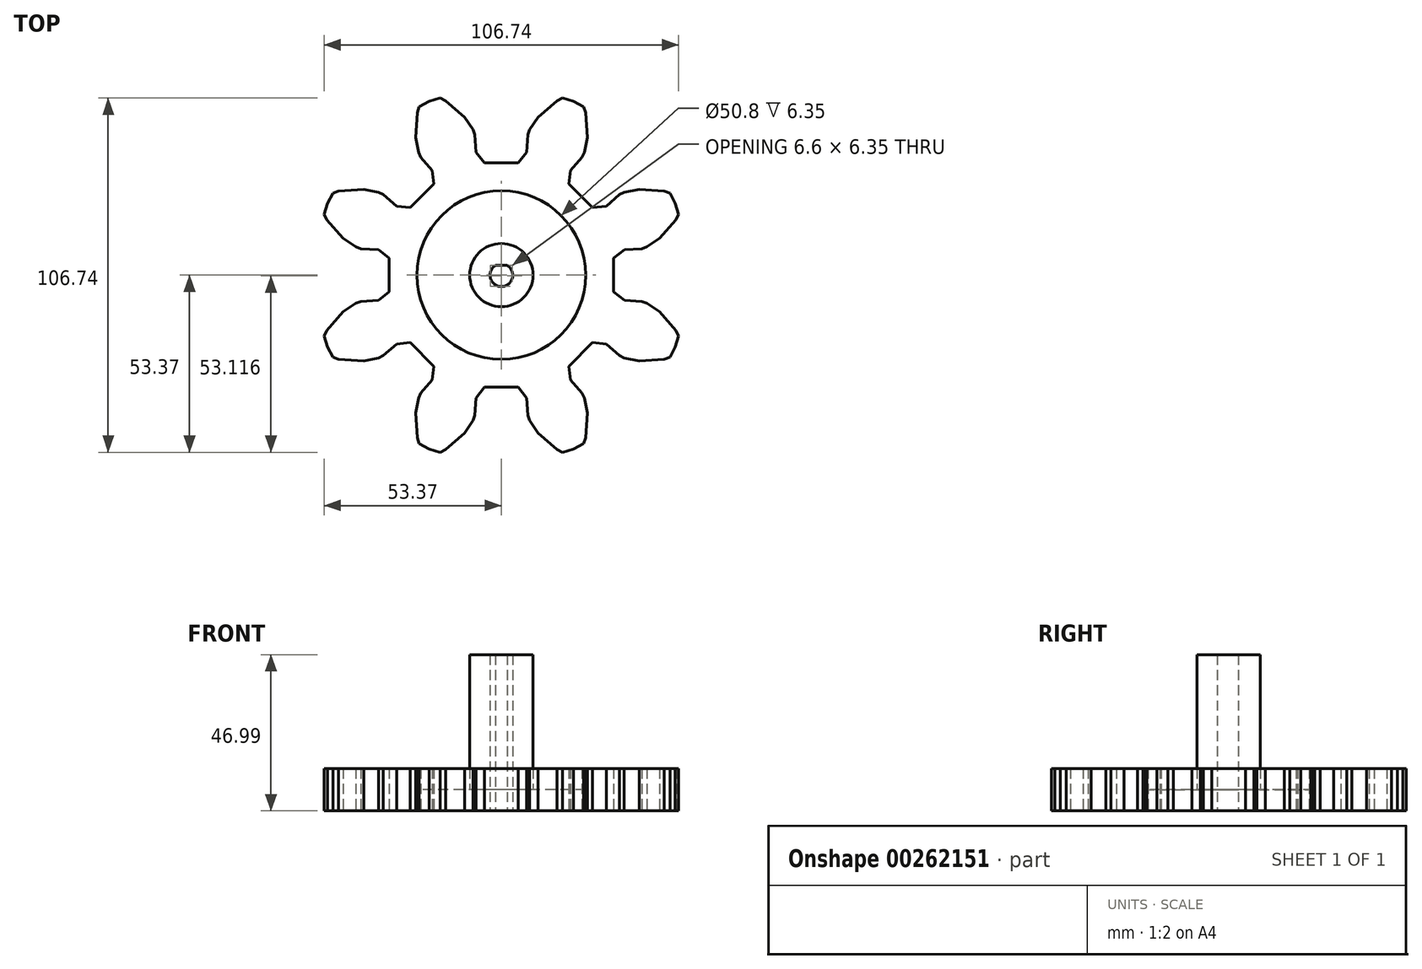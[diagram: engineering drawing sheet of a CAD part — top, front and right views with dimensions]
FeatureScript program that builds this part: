
annotation { "Feature Type Name" : "Feature", "Feature Type Description" : "" }
export const myFeature = defineFeature(function(context is Context, id is Id, definition is map)
    precondition{}
    {
        {
            var Q0;
            Q0=qCreatedBy(makeId("Top.planeOp"),FACE);
            var sketch = newSketch(context, id + "F0", { "sketchPlane" : qUnion([Q0])});
            skLineSegment(sketch, "E0", {"start": v(-50.73, 24.75) * mm, "end": v(-52.36, 21.69) * mm});
            skLineSegment(sketch, "E1", {"start": v(-52.36, 21.69) * mm, "end": v(-53.37, 18.37) * mm});
            skLineSegment(sketch, "E2", {"start": v(-53.37, 18.37) * mm, "end": v(-52.56, 16.72) * mm});
            skLineSegment(sketch, "E3", {"start": v(-52.56, 16.72) * mm, "end": v(-47.6, 11.05) * mm});
            skLineSegment(sketch, "E4", {"start": v(-47.6, 11.05) * mm, "end": v(-43.8, 8.5) * mm});
            skLineSegment(sketch, "E5", {"start": v(-43.8, 8.5) * mm, "end": v(-42.28, 7.97) * mm});
            skLineSegment(sketch, "E6", {"start": v(-42.28, 7.97) * mm, "end": v(-37.01, 7.62) * mm});
            skLineSegment(sketch, "E7", {"start": v(-37.01, 7.62) * mm, "end": v(-33.78, 5.07) * mm});
            skLineSegment(sketch, "E8", {"start": v(-33.78, 5.07) * mm, "end": v(-33.78, -5.07) * mm});
            skLineSegment(sketch, "E9", {"start": v(-33.78, -5.07) * mm, "end": v(-37.01, -7.62) * mm});
            skLineSegment(sketch, "E10", {"start": v(-37.01, -7.62) * mm, "end": v(-42.28, -7.97) * mm});
            skLineSegment(sketch, "E11", {"start": v(-42.28, -7.97) * mm, "end": v(-43.8, -8.5) * mm});
            skLineSegment(sketch, "E12", {"start": v(-43.8, -8.5) * mm, "end": v(-47.6, -11.05) * mm});
            skLineSegment(sketch, "E13", {"start": v(-47.6, -11.05) * mm, "end": v(-52.56, -16.72) * mm});
            skLineSegment(sketch, "E14", {"start": v(-52.56, -16.72) * mm, "end": v(-53.37, -18.37) * mm});
            skLineSegment(sketch, "E15", {"start": v(-53.37, -18.37) * mm, "end": v(-52.36, -21.69) * mm});
            skLineSegment(sketch, "E16", {"start": v(-52.36, -21.69) * mm, "end": v(-50.73, -24.75) * mm});
            skLineSegment(sketch, "E17", {"start": v(-50.73, -24.75) * mm, "end": v(-48.99, -25.34) * mm});
            skLineSegment(sketch, "E18", {"start": v(-48.99, -25.34) * mm, "end": v(-41.47, -25.85) * mm});
            skLineSegment(sketch, "E19", {"start": v(-41.47, -25.85) * mm, "end": v(-36.99, -24.97) * mm});
            skLineSegment(sketch, "E20", {"start": v(-36.99, -24.97) * mm, "end": v(-35.54, -24.26) * mm});
            skLineSegment(sketch, "E21", {"start": v(-35.54, -24.26) * mm, "end": v(-31.56, -20.79) * mm});
            skLineSegment(sketch, "E22", {"start": v(-31.56, -20.79) * mm, "end": v(-27.47, -20.3) * mm});
            skLineSegment(sketch, "E23", {"start": v(-27.47, -20.3) * mm, "end": v(-20.3, -27.47) * mm});
            skLineSegment(sketch, "E24", {"start": v(-20.3, -27.47) * mm, "end": v(-20.79, -31.56) * mm});
            skLineSegment(sketch, "E25", {"start": v(-20.79, -31.56) * mm, "end": v(-24.26, -35.54) * mm});
            skLineSegment(sketch, "E26", {"start": v(-24.26, -35.54) * mm, "end": v(-24.97, -36.99) * mm});
            skLineSegment(sketch, "E27", {"start": v(-24.97, -36.99) * mm, "end": v(-25.85, -41.47) * mm});
            skLineSegment(sketch, "E28", {"start": v(-25.85, -41.47) * mm, "end": v(-25.34, -48.99) * mm});
            skLineSegment(sketch, "E29", {"start": v(-25.34, -48.99) * mm, "end": v(-24.75, -50.73) * mm});
            skLineSegment(sketch, "E30", {"start": v(-24.75, -50.73) * mm, "end": v(-21.69, -52.36) * mm});
            skLineSegment(sketch, "E31", {"start": v(-21.69, -52.36) * mm, "end": v(-18.37, -53.37) * mm});
            skLineSegment(sketch, "E32", {"start": v(-18.37, -53.37) * mm, "end": v(-16.72, -52.56) * mm});
            skLineSegment(sketch, "E33", {"start": v(-16.72, -52.56) * mm, "end": v(-11.05, -47.6) * mm});
            skLineSegment(sketch, "E34", {"start": v(-11.05, -47.6) * mm, "end": v(-8.5, -43.8) * mm});
            skLineSegment(sketch, "E35", {"start": v(-8.5, -43.8) * mm, "end": v(-7.97, -42.28) * mm});
            skLineSegment(sketch, "E36", {"start": v(-7.97, -42.28) * mm, "end": v(-7.62, -37.01) * mm});
            skLineSegment(sketch, "E37", {"start": v(-7.62, -37.01) * mm, "end": v(-5.07, -33.78) * mm});
            skLineSegment(sketch, "E38", {"start": v(-5.07, -33.78) * mm, "end": v(5.07, -33.78) * mm});
            skLineSegment(sketch, "E39", {"start": v(5.07, -33.78) * mm, "end": v(7.62, -37.01) * mm});
            skLineSegment(sketch, "E40", {"start": v(7.62, -37.01) * mm, "end": v(7.97, -42.28) * mm});
            skLineSegment(sketch, "E41", {"start": v(7.97, -42.28) * mm, "end": v(8.5, -43.8) * mm});
            skLineSegment(sketch, "E42", {"start": v(8.5, -43.8) * mm, "end": v(11.05, -47.6) * mm});
            skLineSegment(sketch, "E43", {"start": v(11.05, -47.6) * mm, "end": v(16.72, -52.56) * mm});
            skLineSegment(sketch, "E44", {"start": v(16.72, -52.56) * mm, "end": v(18.37, -53.37) * mm});
            skLineSegment(sketch, "E45", {"start": v(18.37, -53.37) * mm, "end": v(21.69, -52.36) * mm});
            skLineSegment(sketch, "E46", {"start": v(21.69, -52.36) * mm, "end": v(24.75, -50.73) * mm});
            skLineSegment(sketch, "E47", {"start": v(24.75, -50.73) * mm, "end": v(25.34, -48.99) * mm});
            skLineSegment(sketch, "E48", {"start": v(25.34, -48.99) * mm, "end": v(25.85, -41.47) * mm});
            skLineSegment(sketch, "E49", {"start": v(25.85, -41.47) * mm, "end": v(24.97, -36.99) * mm});
            skLineSegment(sketch, "E50", {"start": v(24.97, -36.99) * mm, "end": v(24.26, -35.54) * mm});
            skLineSegment(sketch, "E51", {"start": v(24.26, -35.54) * mm, "end": v(20.79, -31.56) * mm});
            skLineSegment(sketch, "E52", {"start": v(20.79, -31.56) * mm, "end": v(20.3, -27.47) * mm});
            skLineSegment(sketch, "E53", {"start": v(20.3, -27.47) * mm, "end": v(27.47, -20.3) * mm});
            skLineSegment(sketch, "E54", {"start": v(27.47, -20.3) * mm, "end": v(31.56, -20.79) * mm});
            skLineSegment(sketch, "E55", {"start": v(31.56, -20.79) * mm, "end": v(35.54, -24.26) * mm});
            skLineSegment(sketch, "E56", {"start": v(35.54, -24.26) * mm, "end": v(36.99, -24.97) * mm});
            skLineSegment(sketch, "E57", {"start": v(36.99, -24.97) * mm, "end": v(41.47, -25.85) * mm});
            skLineSegment(sketch, "E58", {"start": v(41.47, -25.85) * mm, "end": v(48.99, -25.34) * mm});
            skLineSegment(sketch, "E59", {"start": v(48.99, -25.34) * mm, "end": v(50.73, -24.75) * mm});
            skLineSegment(sketch, "E60", {"start": v(50.73, -24.75) * mm, "end": v(52.36, -21.69) * mm});
            skLineSegment(sketch, "E61", {"start": v(52.36, -21.69) * mm, "end": v(53.37, -18.37) * mm});
            skLineSegment(sketch, "E62", {"start": v(53.37, -18.37) * mm, "end": v(52.56, -16.72) * mm});
            skLineSegment(sketch, "E63", {"start": v(52.56, -16.72) * mm, "end": v(47.6, -11.05) * mm});
            skLineSegment(sketch, "E64", {"start": v(47.6, -11.05) * mm, "end": v(43.8, -8.5) * mm});
            skLineSegment(sketch, "E65", {"start": v(43.8, -8.5) * mm, "end": v(42.28, -7.97) * mm});
            skLineSegment(sketch, "E66", {"start": v(42.28, -7.97) * mm, "end": v(37.01, -7.62) * mm});
            skLineSegment(sketch, "E67", {"start": v(37.01, -7.62) * mm, "end": v(33.78, -5.07) * mm});
            skLineSegment(sketch, "E68", {"start": v(33.78, -5.07) * mm, "end": v(33.78, 5.07) * mm});
            skLineSegment(sketch, "E69", {"start": v(33.78, 5.07) * mm, "end": v(37.01, 7.62) * mm});
            skLineSegment(sketch, "E70", {"start": v(37.01, 7.62) * mm, "end": v(42.28, 7.97) * mm});
            skLineSegment(sketch, "E71", {"start": v(42.28, 7.97) * mm, "end": v(43.8, 8.5) * mm});
            skLineSegment(sketch, "E72", {"start": v(43.8, 8.5) * mm, "end": v(47.6, 11.05) * mm});
            skLineSegment(sketch, "E73", {"start": v(47.6, 11.05) * mm, "end": v(52.56, 16.72) * mm});
            skLineSegment(sketch, "E74", {"start": v(52.56, 16.72) * mm, "end": v(53.37, 18.37) * mm});
            skLineSegment(sketch, "E75", {"start": v(53.37, 18.37) * mm, "end": v(52.36, 21.69) * mm});
            skLineSegment(sketch, "E76", {"start": v(52.36, 21.69) * mm, "end": v(50.73, 24.75) * mm});
            skLineSegment(sketch, "E77", {"start": v(50.73, 24.75) * mm, "end": v(48.99, 25.34) * mm});
            skLineSegment(sketch, "E78", {"start": v(48.99, 25.34) * mm, "end": v(41.47, 25.85) * mm});
            skLineSegment(sketch, "E79", {"start": v(41.47, 25.85) * mm, "end": v(36.99, 24.97) * mm});
            skLineSegment(sketch, "E80", {"start": v(36.99, 24.97) * mm, "end": v(35.54, 24.26) * mm});
            skLineSegment(sketch, "E81", {"start": v(35.54, 24.26) * mm, "end": v(31.56, 20.79) * mm});
            skLineSegment(sketch, "E82", {"start": v(31.56, 20.79) * mm, "end": v(27.47, 20.3) * mm});
            skLineSegment(sketch, "E83", {"start": v(27.47, 20.3) * mm, "end": v(20.3, 27.47) * mm});
            skLineSegment(sketch, "E84", {"start": v(20.3, 27.47) * mm, "end": v(20.79, 31.56) * mm});
            skLineSegment(sketch, "E85", {"start": v(20.79, 31.56) * mm, "end": v(24.26, 35.54) * mm});
            skLineSegment(sketch, "E86", {"start": v(24.26, 35.54) * mm, "end": v(24.97, 36.99) * mm});
            skLineSegment(sketch, "E87", {"start": v(24.97, 36.99) * mm, "end": v(25.85, 41.47) * mm});
            skLineSegment(sketch, "E88", {"start": v(25.85, 41.47) * mm, "end": v(25.34, 48.99) * mm});
            skLineSegment(sketch, "E89", {"start": v(25.34, 48.99) * mm, "end": v(24.75, 50.73) * mm});
            skLineSegment(sketch, "E90", {"start": v(24.75, 50.73) * mm, "end": v(21.69, 52.36) * mm});
            skLineSegment(sketch, "E91", {"start": v(21.69, 52.36) * mm, "end": v(18.37, 53.37) * mm});
            skLineSegment(sketch, "E92", {"start": v(18.37, 53.37) * mm, "end": v(16.72, 52.56) * mm});
            skLineSegment(sketch, "E93", {"start": v(16.72, 52.56) * mm, "end": v(11.05, 47.6) * mm});
            skLineSegment(sketch, "E94", {"start": v(11.05, 47.6) * mm, "end": v(8.5, 43.8) * mm});
            skLineSegment(sketch, "E95", {"start": v(8.5, 43.8) * mm, "end": v(7.97, 42.28) * mm});
            skLineSegment(sketch, "E96", {"start": v(7.97, 42.28) * mm, "end": v(7.62, 37.01) * mm});
            skLineSegment(sketch, "E97", {"start": v(7.62, 37.01) * mm, "end": v(5.07, 33.78) * mm});
            skLineSegment(sketch, "E98", {"start": v(5.07, 33.78) * mm, "end": v(-5.07, 33.78) * mm});
            skLineSegment(sketch, "E99", {"start": v(-5.07, 33.78) * mm, "end": v(-7.62, 37.01) * mm});
            skLineSegment(sketch, "E100", {"start": v(-7.62, 37.01) * mm, "end": v(-7.97, 42.28) * mm});
            skLineSegment(sketch, "E101", {"start": v(-7.97, 42.28) * mm, "end": v(-8.5, 43.8) * mm});
            skLineSegment(sketch, "E102", {"start": v(-8.5, 43.8) * mm, "end": v(-11.05, 47.6) * mm});
            skLineSegment(sketch, "E103", {"start": v(-11.05, 47.6) * mm, "end": v(-16.72, 52.56) * mm});
            skLineSegment(sketch, "E104", {"start": v(-16.72, 52.56) * mm, "end": v(-18.37, 53.37) * mm});
            skLineSegment(sketch, "E105", {"start": v(-18.37, 53.37) * mm, "end": v(-21.69, 52.36) * mm});
            skLineSegment(sketch, "E106", {"start": v(-21.69, 52.36) * mm, "end": v(-24.75, 50.73) * mm});
            skLineSegment(sketch, "E107", {"start": v(-24.75, 50.73) * mm, "end": v(-25.34, 48.99) * mm});
            skLineSegment(sketch, "E108", {"start": v(-25.34, 48.99) * mm, "end": v(-25.85, 41.47) * mm});
            skLineSegment(sketch, "E109", {"start": v(-25.85, 41.47) * mm, "end": v(-24.97, 36.99) * mm});
            skLineSegment(sketch, "E110", {"start": v(-24.97, 36.99) * mm, "end": v(-24.26, 35.54) * mm});
            skLineSegment(sketch, "E111", {"start": v(-24.26, 35.54) * mm, "end": v(-20.79, 31.56) * mm});
            skLineSegment(sketch, "E112", {"start": v(-20.79, 31.56) * mm, "end": v(-20.3, 27.47) * mm});
            skLineSegment(sketch, "E113", {"start": v(-20.3, 27.47) * mm, "end": v(-27.47, 20.3) * mm});
            skLineSegment(sketch, "E114", {"start": v(-27.47, 20.3) * mm, "end": v(-31.56, 20.79) * mm});
            skLineSegment(sketch, "E115", {"start": v(-31.56, 20.79) * mm, "end": v(-35.54, 24.26) * mm});
            skLineSegment(sketch, "E116", {"start": v(-35.54, 24.26) * mm, "end": v(-36.99, 24.97) * mm});
            skLineSegment(sketch, "E117", {"start": v(-36.99, 24.97) * mm, "end": v(-41.47, 25.85) * mm});
            skLineSegment(sketch, "E118", {"start": v(-41.47, 25.85) * mm, "end": v(-48.99, 25.34) * mm});
            skLineSegment(sketch, "E119", {"start": v(-48.99, 25.34) * mm, "end": v(-50.73, 24.75) * mm});
            skLineSegment(sketch, "E120", {"start": v(-5.04, 7.34) * mm, "end": v(-3.4, 8.22) * mm});
            skLineSegment(sketch, "E121", {"start": v(-3.4, 8.22) * mm, "end": v(-1.62, 8.75) * mm});
            skLineSegment(sketch, "E122", {"start": v(-1.62, 8.75) * mm, "end": v(0.23, 8.9) * mm});
            skLineSegment(sketch, "E123", {"start": v(0.23, 8.9) * mm, "end": v(2.08, 8.66) * mm});
            skLineSegment(sketch, "E124", {"start": v(2.08, 8.66) * mm, "end": v(3.83, 8.04) * mm});
            skLineSegment(sketch, "E125", {"start": v(3.83, 8.04) * mm, "end": v(5.42, 7.06) * mm});
            skLineSegment(sketch, "E126", {"start": v(5.42, 7.06) * mm, "end": v(6.77, 5.78) * mm});
            skLineSegment(sketch, "E127", {"start": v(6.77, 5.78) * mm, "end": v(7.82, 4.25) * mm});
            skLineSegment(sketch, "E128", {"start": v(7.82, 4.25) * mm, "end": v(8.54, 2.53) * mm});
            skLineSegment(sketch, "E129", {"start": v(8.54, 2.53) * mm, "end": v(8.87, 0.7) * mm});
            skLineSegment(sketch, "E130", {"start": v(8.87, 0.7) * mm, "end": v(8.83, -1.16) * mm});
            skLineSegment(sketch, "E131", {"start": v(8.83, -1.16) * mm, "end": v(8.4, -2.97) * mm});
            skLineSegment(sketch, "E132", {"start": v(8.4, -2.97) * mm, "end": v(7.6, -4.65) * mm});
            skLineSegment(sketch, "E133", {"start": v(7.6, -4.65) * mm, "end": v(6.46, -6.13) * mm});
            skLineSegment(sketch, "E134", {"start": v(6.46, -6.13) * mm, "end": v(5.04, -7.34) * mm});
            skLineSegment(sketch, "E135", {"start": v(5.04, -7.34) * mm, "end": v(3.4, -8.22) * mm});
            skLineSegment(sketch, "E136", {"start": v(3.4, -8.22) * mm, "end": v(1.62, -8.75) * mm});
            skLineSegment(sketch, "E137", {"start": v(1.62, -8.75) * mm, "end": v(-0.23, -8.9) * mm});
            skLineSegment(sketch, "E138", {"start": v(-0.23, -8.9) * mm, "end": v(-2.08, -8.66) * mm});
            skLineSegment(sketch, "E139", {"start": v(-2.08, -8.66) * mm, "end": v(-3.83, -8.04) * mm});
            skLineSegment(sketch, "E140", {"start": v(-3.83, -8.04) * mm, "end": v(-5.42, -7.06) * mm});
            skLineSegment(sketch, "E141", {"start": v(-5.42, -7.06) * mm, "end": v(-6.77, -5.78) * mm});
            skLineSegment(sketch, "E142", {"start": v(-6.77, -5.78) * mm, "end": v(-7.82, -4.25) * mm});
            skLineSegment(sketch, "E143", {"start": v(-7.82, -4.25) * mm, "end": v(-8.54, -2.53) * mm});
            skLineSegment(sketch, "E144", {"start": v(-8.54, -2.53) * mm, "end": v(-8.87, -0.7) * mm});
            skLineSegment(sketch, "E145", {"start": v(-8.87, -0.7) * mm, "end": v(-8.83, 1.16) * mm});
            skLineSegment(sketch, "E146", {"start": v(-8.83, 1.16) * mm, "end": v(-8.4, 2.97) * mm});
            skLineSegment(sketch, "E147", {"start": v(-8.4, 2.97) * mm, "end": v(-7.6, 4.65) * mm});
            skLineSegment(sketch, "E148", {"start": v(-7.6, 4.65) * mm, "end": v(-6.46, 6.13) * mm});
            skLineSegment(sketch, "E149", {"start": v(-6.46, 6.13) * mm, "end": v(-5.04, 7.34) * mm});
            skSolve(sketch);
        }
        {
            var Q0;
            Q0=makeQuery(id+"F0.imprint","IMPRINT",FACE,{"disambiguationData":[TD([[makeQuery(id+"F0.imprint","IMPRINT",EDGE,{"derivedFrom":sQuery(id+"F0.wireOp",EDGE,"E0")}),1.0]])]});
            var Q1;
            Q1=makeQuery(id+"F0.imprint","IMPRINT",FACE,{"disambiguationData":[TD([[makeQuery(id+"F0.imprint","IMPRINT",EDGE,{"derivedFrom":sQuery(id+"F0.wireOp",EDGE,"E120")}),-1.0]])]});
            extrude(context, id + "F1", {"entities" : qUnion([Q0, Q1]), "depth" : 12.7 * mm, "offsetDistance" : 25.4 * mm});
        }
        {
            var Q0;
            Q0=makeQuery(id+"F1.opExtrude","CAP_FACE",FACE,{"disambiguationData":[OSD([sQuery(id+"F0.wireOp",EDGE,"E0"),sQuery(id+"F0.wireOp",EDGE,"E1"),sQuery(id+"F0.wireOp",EDGE,"E2"),sQuery(id+"F0.wireOp",EDGE,"E3"),sQuery(id+"F0.wireOp",EDGE,"E4"),sQuery(id+"F0.wireOp",EDGE,"E5"),sQuery(id+"F0.wireOp",EDGE,"E6"),sQuery(id+"F0.wireOp",EDGE,"E7"),sQuery(id+"F0.wireOp",EDGE,"E8"),sQuery(id+"F0.wireOp",EDGE,"E9"),sQuery(id+"F0.wireOp",EDGE,"E10"),sQuery(id+"F0.wireOp",EDGE,"E11"),sQuery(id+"F0.wireOp",EDGE,"E12"),sQuery(id+"F0.wireOp",EDGE,"E13"),sQuery(id+"F0.wireOp",EDGE,"E14"),sQuery(id+"F0.wireOp",EDGE,"E15"),sQuery(id+"F0.wireOp",EDGE,"E16"),sQuery(id+"F0.wireOp",EDGE,"E17"),sQuery(id+"F0.wireOp",EDGE,"E18"),sQuery(id+"F0.wireOp",EDGE,"E19"),sQuery(id+"F0.wireOp",EDGE,"E20"),sQuery(id+"F0.wireOp",EDGE,"E21"),sQuery(id+"F0.wireOp",EDGE,"E22"),sQuery(id+"F0.wireOp",EDGE,"E23"),sQuery(id+"F0.wireOp",EDGE,"E24"),sQuery(id+"F0.wireOp",EDGE,"E25"),sQuery(id+"F0.wireOp",EDGE,"E26"),sQuery(id+"F0.wireOp",EDGE,"E27"),sQuery(id+"F0.wireOp",EDGE,"E28"),sQuery(id+"F0.wireOp",EDGE,"E29"),sQuery(id+"F0.wireOp",EDGE,"E30"),sQuery(id+"F0.wireOp",EDGE,"E31"),sQuery(id+"F0.wireOp",EDGE,"E32"),sQuery(id+"F0.wireOp",EDGE,"E33"),sQuery(id+"F0.wireOp",EDGE,"E34"),sQuery(id+"F0.wireOp",EDGE,"E35"),sQuery(id+"F0.wireOp",EDGE,"E36"),sQuery(id+"F0.wireOp",EDGE,"E37"),sQuery(id+"F0.wireOp",EDGE,"E38"),sQuery(id+"F0.wireOp",EDGE,"E39"),sQuery(id+"F0.wireOp",EDGE,"E40"),sQuery(id+"F0.wireOp",EDGE,"E41"),sQuery(id+"F0.wireOp",EDGE,"E42"),sQuery(id+"F0.wireOp",EDGE,"E43"),sQuery(id+"F0.wireOp",EDGE,"E44"),sQuery(id+"F0.wireOp",EDGE,"E45"),sQuery(id+"F0.wireOp",EDGE,"E46"),sQuery(id+"F0.wireOp",EDGE,"E47"),sQuery(id+"F0.wireOp",EDGE,"E48"),sQuery(id+"F0.wireOp",EDGE,"E49"),sQuery(id+"F0.wireOp",EDGE,"E50"),sQuery(id+"F0.wireOp",EDGE,"E51"),sQuery(id+"F0.wireOp",EDGE,"E52"),sQuery(id+"F0.wireOp",EDGE,"E53"),sQuery(id+"F0.wireOp",EDGE,"E54"),sQuery(id+"F0.wireOp",EDGE,"E55"),sQuery(id+"F0.wireOp",EDGE,"E56"),sQuery(id+"F0.wireOp",EDGE,"E57"),sQuery(id+"F0.wireOp",EDGE,"E58"),sQuery(id+"F0.wireOp",EDGE,"E59"),sQuery(id+"F0.wireOp",EDGE,"E60"),sQuery(id+"F0.wireOp",EDGE,"E61"),sQuery(id+"F0.wireOp",EDGE,"E62"),sQuery(id+"F0.wireOp",EDGE,"E63"),sQuery(id+"F0.wireOp",EDGE,"E64"),sQuery(id+"F0.wireOp",EDGE,"E65"),sQuery(id+"F0.wireOp",EDGE,"E66"),sQuery(id+"F0.wireOp",EDGE,"E67"),sQuery(id+"F0.wireOp",EDGE,"E68"),sQuery(id+"F0.wireOp",EDGE,"E69"),sQuery(id+"F0.wireOp",EDGE,"E70"),sQuery(id+"F0.wireOp",EDGE,"E71"),sQuery(id+"F0.wireOp",EDGE,"E72"),sQuery(id+"F0.wireOp",EDGE,"E73"),sQuery(id+"F0.wireOp",EDGE,"E74"),sQuery(id+"F0.wireOp",EDGE,"E75"),sQuery(id+"F0.wireOp",EDGE,"E76"),sQuery(id+"F0.wireOp",EDGE,"E77"),sQuery(id+"F0.wireOp",EDGE,"E78"),sQuery(id+"F0.wireOp",EDGE,"E79"),sQuery(id+"F0.wireOp",EDGE,"E80"),sQuery(id+"F0.wireOp",EDGE,"E81"),sQuery(id+"F0.wireOp",EDGE,"E82"),sQuery(id+"F0.wireOp",EDGE,"E83"),sQuery(id+"F0.wireOp",EDGE,"E84"),sQuery(id+"F0.wireOp",EDGE,"E85"),sQuery(id+"F0.wireOp",EDGE,"E86"),sQuery(id+"F0.wireOp",EDGE,"E87"),sQuery(id+"F0.wireOp",EDGE,"E88"),sQuery(id+"F0.wireOp",EDGE,"E89"),sQuery(id+"F0.wireOp",EDGE,"E90"),sQuery(id+"F0.wireOp",EDGE,"E91"),sQuery(id+"F0.wireOp",EDGE,"E92"),sQuery(id+"F0.wireOp",EDGE,"E93"),sQuery(id+"F0.wireOp",EDGE,"E94"),sQuery(id+"F0.wireOp",EDGE,"E95"),sQuery(id+"F0.wireOp",EDGE,"E96"),sQuery(id+"F0.wireOp",EDGE,"E97"),sQuery(id+"F0.wireOp",EDGE,"E98"),sQuery(id+"F0.wireOp",EDGE,"E99"),sQuery(id+"F0.wireOp",EDGE,"E100"),sQuery(id+"F0.wireOp",EDGE,"E101"),sQuery(id+"F0.wireOp",EDGE,"E102"),sQuery(id+"F0.wireOp",EDGE,"E103"),sQuery(id+"F0.wireOp",EDGE,"E104"),sQuery(id+"F0.wireOp",EDGE,"E105"),sQuery(id+"F0.wireOp",EDGE,"E106"),sQuery(id+"F0.wireOp",EDGE,"E107"),sQuery(id+"F0.wireOp",EDGE,"E108"),sQuery(id+"F0.wireOp",EDGE,"E109"),sQuery(id+"F0.wireOp",EDGE,"E110"),sQuery(id+"F0.wireOp",EDGE,"E111"),sQuery(id+"F0.wireOp",EDGE,"E112"),sQuery(id+"F0.wireOp",EDGE,"E113"),sQuery(id+"F0.wireOp",EDGE,"E114"),sQuery(id+"F0.wireOp",EDGE,"E115"),sQuery(id+"F0.wireOp",EDGE,"E116"),sQuery(id+"F0.wireOp",EDGE,"E117"),sQuery(id+"F0.wireOp",EDGE,"E118"),sQuery(id+"F0.wireOp",EDGE,"E119")])],"isStart":false});
            var sketch = newSketch(context, id + "F2", { "sketchPlane" : qUnion([Q0])});
            skCircle(sketch, "E150", {"center": v(0, 0) * mm, "radius": 3.43 * mm});
            skLineSegment(sketch, "E151", {"start": v(4.59, 2.92) * mm, "end": v(-4.97, 2.92) * mm});
            skCircle(sketch, "E152", {"center": v(0, 0) * mm, "radius": 9.53 * mm});
            skCircle(sketch, "E153", {"center": v(0, 0) * mm, "radius": 25.4 * mm});
            skSolve(sketch);
        }
        {
            var Q0;
            Q0=makeQuery(id+"F2.imprint","IMPRINT",FACE,{"disambiguationData":[TD([[makeQuery(id+"F2.imprint","IMPRINT",EDGE,{"derivedFrom":sQuery(id+"F2.wireOp",EDGE,"E152")}),1.0]])]});
            var Q1;
            {var subQ0=sQuery(id+"F2.wireOp",EDGE,"E151");var subQ1=sQuery(id+"F2.wireOp",EDGE,"E150");var subQ2=makeQuery(id+"F2.imprint","INTERSECT",VERTEX,{"disambiguationData":[OD(0.0)],"derivedFrom":[subQ1,subQ0]});Q1=makeQuery(id+"F2.imprint","IMPRINT",FACE,{"disambiguationData":[TD([[makeQuery(id+"F2.imprint","IMPRINT",EDGE,{"disambiguationData":[TD([[subQ2,1.0]])],"derivedFrom":subQ1}),1.0]])]});}
            extrude(context, id + "F3", {"entities" : qUnion([Q0, Q1]), "operationType" : NewBodyOperationType.ADD, "depth" : 34.3 * mm, "offsetDistance" : 25.4 * mm});
        }
        {
            var Q0;
            Q0=makeQuery(id+"F3.boolean.opBoolean","SPLIT",FACE,{"disambiguationData":[TD([makeQuery(id+"F3.opExtrude","SWEPT_FACE",FACE,{"disambiguationData":[OSD([sQuery(id+"F2.wireOp",EDGE,"E150")])]})])],"derivedFrom":makeQuery(id+"F1.opExtrude","CAP_FACE",FACE,{"disambiguationData":[OSD([sQuery(id+"F0.wireOp",EDGE,"E0"),sQuery(id+"F0.wireOp",EDGE,"E1"),sQuery(id+"F0.wireOp",EDGE,"E2"),sQuery(id+"F0.wireOp",EDGE,"E3"),sQuery(id+"F0.wireOp",EDGE,"E4"),sQuery(id+"F0.wireOp",EDGE,"E5"),sQuery(id+"F0.wireOp",EDGE,"E6"),sQuery(id+"F0.wireOp",EDGE,"E7"),sQuery(id+"F0.wireOp",EDGE,"E8"),sQuery(id+"F0.wireOp",EDGE,"E9"),sQuery(id+"F0.wireOp",EDGE,"E10"),sQuery(id+"F0.wireOp",EDGE,"E11"),sQuery(id+"F0.wireOp",EDGE,"E12"),sQuery(id+"F0.wireOp",EDGE,"E13"),sQuery(id+"F0.wireOp",EDGE,"E14"),sQuery(id+"F0.wireOp",EDGE,"E15"),sQuery(id+"F0.wireOp",EDGE,"E16"),sQuery(id+"F0.wireOp",EDGE,"E17"),sQuery(id+"F0.wireOp",EDGE,"E18"),sQuery(id+"F0.wireOp",EDGE,"E19"),sQuery(id+"F0.wireOp",EDGE,"E20"),sQuery(id+"F0.wireOp",EDGE,"E21"),sQuery(id+"F0.wireOp",EDGE,"E22"),sQuery(id+"F0.wireOp",EDGE,"E23"),sQuery(id+"F0.wireOp",EDGE,"E24"),sQuery(id+"F0.wireOp",EDGE,"E25"),sQuery(id+"F0.wireOp",EDGE,"E26"),sQuery(id+"F0.wireOp",EDGE,"E27"),sQuery(id+"F0.wireOp",EDGE,"E28"),sQuery(id+"F0.wireOp",EDGE,"E29"),sQuery(id+"F0.wireOp",EDGE,"E30"),sQuery(id+"F0.wireOp",EDGE,"E31"),sQuery(id+"F0.wireOp",EDGE,"E32"),sQuery(id+"F0.wireOp",EDGE,"E33"),sQuery(id+"F0.wireOp",EDGE,"E34"),sQuery(id+"F0.wireOp",EDGE,"E35"),sQuery(id+"F0.wireOp",EDGE,"E36"),sQuery(id+"F0.wireOp",EDGE,"E37"),sQuery(id+"F0.wireOp",EDGE,"E38"),sQuery(id+"F0.wireOp",EDGE,"E39"),sQuery(id+"F0.wireOp",EDGE,"E40"),sQuery(id+"F0.wireOp",EDGE,"E41"),sQuery(id+"F0.wireOp",EDGE,"E42"),sQuery(id+"F0.wireOp",EDGE,"E43"),sQuery(id+"F0.wireOp",EDGE,"E44"),sQuery(id+"F0.wireOp",EDGE,"E45"),sQuery(id+"F0.wireOp",EDGE,"E46"),sQuery(id+"F0.wireOp",EDGE,"E47"),sQuery(id+"F0.wireOp",EDGE,"E48"),sQuery(id+"F0.wireOp",EDGE,"E49"),sQuery(id+"F0.wireOp",EDGE,"E50"),sQuery(id+"F0.wireOp",EDGE,"E51"),sQuery(id+"F0.wireOp",EDGE,"E52"),sQuery(id+"F0.wireOp",EDGE,"E53"),sQuery(id+"F0.wireOp",EDGE,"E54"),sQuery(id+"F0.wireOp",EDGE,"E55"),sQuery(id+"F0.wireOp",EDGE,"E56"),sQuery(id+"F0.wireOp",EDGE,"E57"),sQuery(id+"F0.wireOp",EDGE,"E58"),sQuery(id+"F0.wireOp",EDGE,"E59"),sQuery(id+"F0.wireOp",EDGE,"E60"),sQuery(id+"F0.wireOp",EDGE,"E61"),sQuery(id+"F0.wireOp",EDGE,"E62"),sQuery(id+"F0.wireOp",EDGE,"E63"),sQuery(id+"F0.wireOp",EDGE,"E64"),sQuery(id+"F0.wireOp",EDGE,"E65"),sQuery(id+"F0.wireOp",EDGE,"E66"),sQuery(id+"F0.wireOp",EDGE,"E67"),sQuery(id+"F0.wireOp",EDGE,"E68"),sQuery(id+"F0.wireOp",EDGE,"E69"),sQuery(id+"F0.wireOp",EDGE,"E70"),sQuery(id+"F0.wireOp",EDGE,"E71"),sQuery(id+"F0.wireOp",EDGE,"E72"),sQuery(id+"F0.wireOp",EDGE,"E73"),sQuery(id+"F0.wireOp",EDGE,"E74"),sQuery(id+"F0.wireOp",EDGE,"E75"),sQuery(id+"F0.wireOp",EDGE,"E76"),sQuery(id+"F0.wireOp",EDGE,"E77"),sQuery(id+"F0.wireOp",EDGE,"E78"),sQuery(id+"F0.wireOp",EDGE,"E79"),sQuery(id+"F0.wireOp",EDGE,"E80"),sQuery(id+"F0.wireOp",EDGE,"E81"),sQuery(id+"F0.wireOp",EDGE,"E82"),sQuery(id+"F0.wireOp",EDGE,"E83"),sQuery(id+"F0.wireOp",EDGE,"E84"),sQuery(id+"F0.wireOp",EDGE,"E85"),sQuery(id+"F0.wireOp",EDGE,"E86"),sQuery(id+"F0.wireOp",EDGE,"E87"),sQuery(id+"F0.wireOp",EDGE,"E88"),sQuery(id+"F0.wireOp",EDGE,"E89"),sQuery(id+"F0.wireOp",EDGE,"E90"),sQuery(id+"F0.wireOp",EDGE,"E91"),sQuery(id+"F0.wireOp",EDGE,"E92"),sQuery(id+"F0.wireOp",EDGE,"E93"),sQuery(id+"F0.wireOp",EDGE,"E94"),sQuery(id+"F0.wireOp",EDGE,"E95"),sQuery(id+"F0.wireOp",EDGE,"E96"),sQuery(id+"F0.wireOp",EDGE,"E97"),sQuery(id+"F0.wireOp",EDGE,"E98"),sQuery(id+"F0.wireOp",EDGE,"E99"),sQuery(id+"F0.wireOp",EDGE,"E100"),sQuery(id+"F0.wireOp",EDGE,"E101"),sQuery(id+"F0.wireOp",EDGE,"E102"),sQuery(id+"F0.wireOp",EDGE,"E103"),sQuery(id+"F0.wireOp",EDGE,"E104"),sQuery(id+"F0.wireOp",EDGE,"E105"),sQuery(id+"F0.wireOp",EDGE,"E106"),sQuery(id+"F0.wireOp",EDGE,"E107"),sQuery(id+"F0.wireOp",EDGE,"E108"),sQuery(id+"F0.wireOp",EDGE,"E109"),sQuery(id+"F0.wireOp",EDGE,"E110"),sQuery(id+"F0.wireOp",EDGE,"E111"),sQuery(id+"F0.wireOp",EDGE,"E112"),sQuery(id+"F0.wireOp",EDGE,"E113"),sQuery(id+"F0.wireOp",EDGE,"E114"),sQuery(id+"F0.wireOp",EDGE,"E115"),sQuery(id+"F0.wireOp",EDGE,"E116"),sQuery(id+"F0.wireOp",EDGE,"E117"),sQuery(id+"F0.wireOp",EDGE,"E118"),sQuery(id+"F0.wireOp",EDGE,"E119")])],"isStart":false})});
            extrude(context, id + "F4", {"entities" : qUnion([Q0]), "operationType" : NewBodyOperationType.REMOVE, "oppositeDirection" : true, "depth" : 25.4 * mm});
        }
        {
            var Q0;
            Q0=makeQuery(id+"F2.imprint","IMPRINT",FACE,{"disambiguationData":[TD([[makeQuery(id+"F2.imprint","IMPRINT",EDGE,{"derivedFrom":sQuery(id+"F2.wireOp",EDGE,"E152")}),-1.0]])]});
            extrude(context, id + "F5", {"entities" : qUnion([Q0]), "operationType" : NewBodyOperationType.REMOVE, "oppositeDirection" : true, "depth" : 6.35 * mm, "offsetDistance" : 25.4 * mm});
        }
    });
